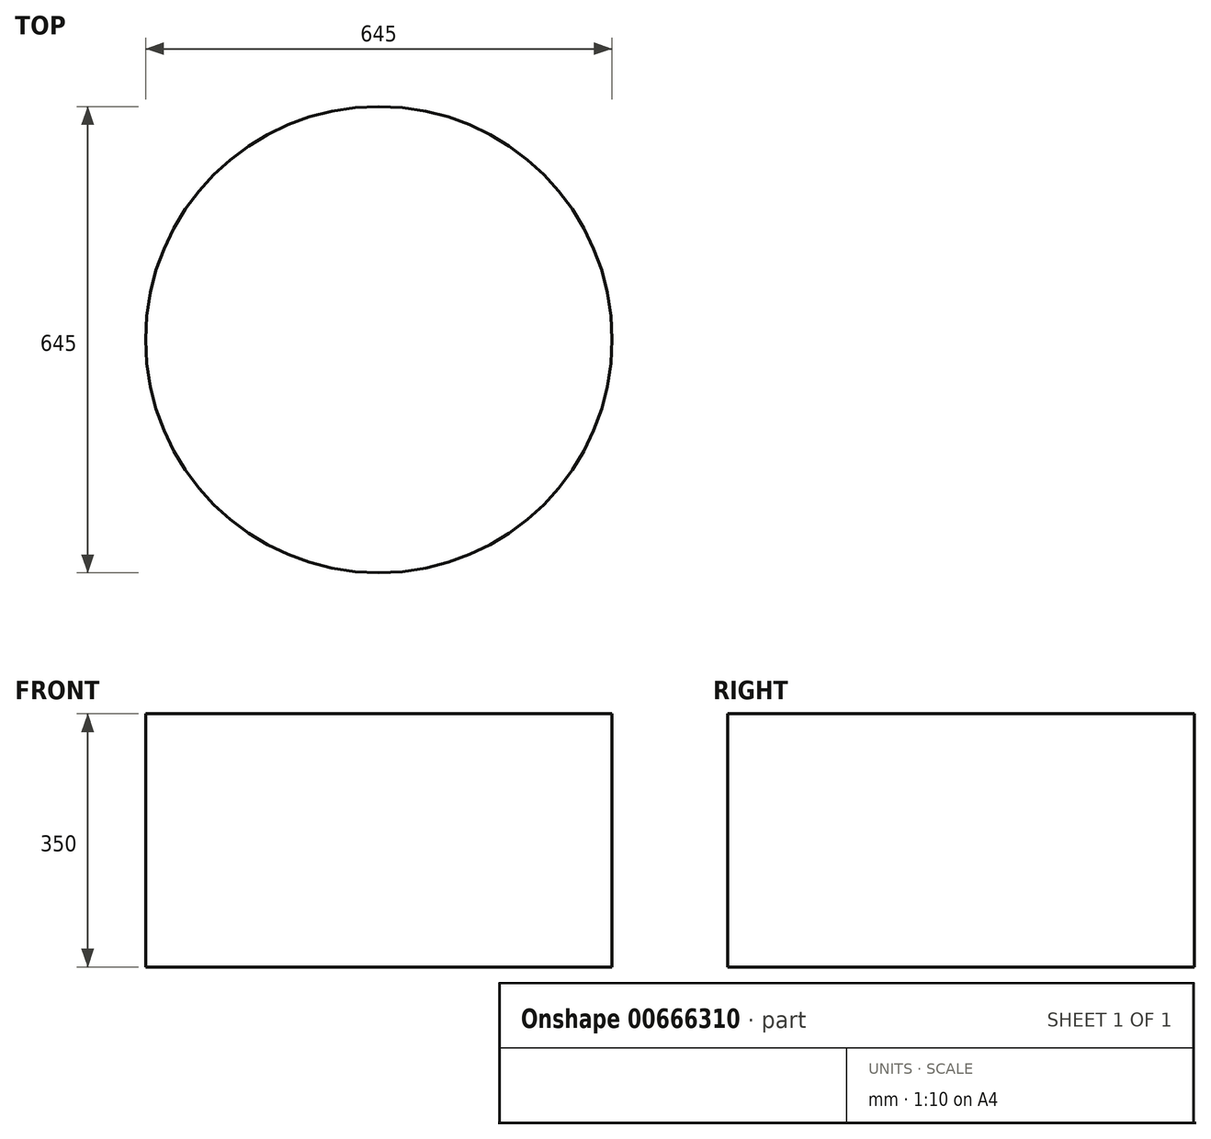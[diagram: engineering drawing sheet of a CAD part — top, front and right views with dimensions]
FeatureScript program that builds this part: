
annotation { "Feature Type Name" : "Feature", "Feature Type Description" : "" }
export const myFeature = defineFeature(function(context is Context, id is Id, definition is map)
    precondition{}
    {
        {
            var Q0;
            Q0=qCreatedBy(makeId("Top.planeOp"),FACE);
            var sketch = newSketch(context, id + "F0", { "sketchPlane" : qUnion([Q0])});
            skCircle(sketch, "E0", {"center": v(0, 0) * mm, "radius": 322.5 * mm});
            skSolve(sketch);
        }
        {
            var Q0;
            Q0=qSketchRegion(id+"F0",true);
            extrude(context, id + "F1", {"entities" : qUnion([Q0]), "depth" : 350 * mm});
        }
    });
